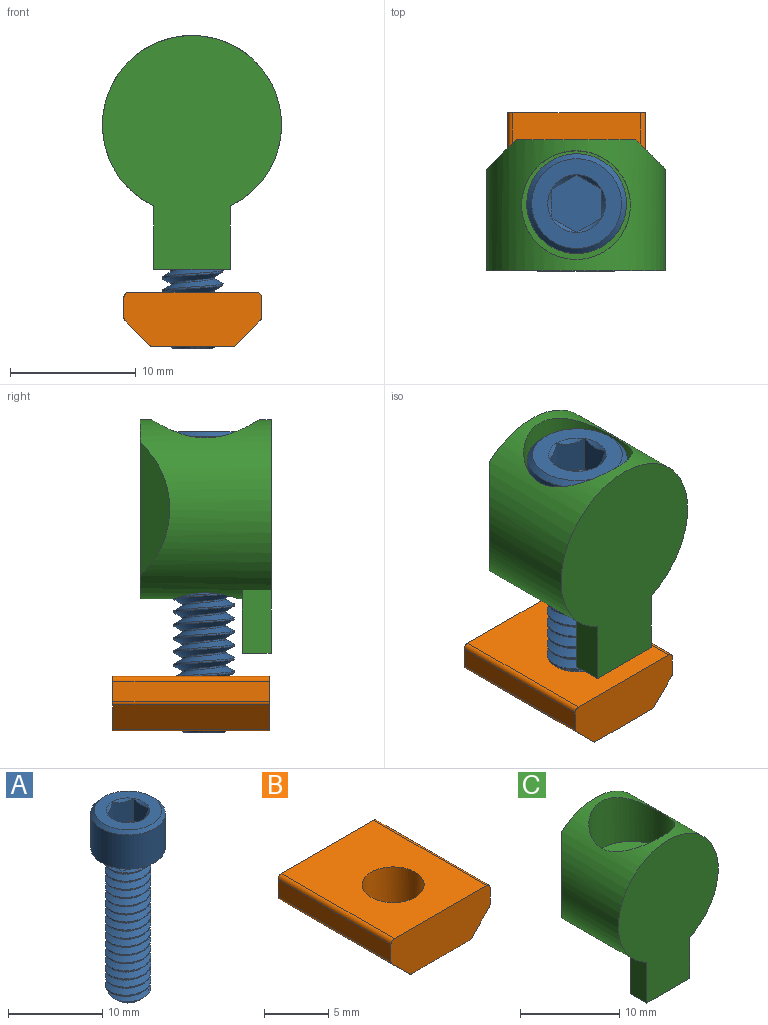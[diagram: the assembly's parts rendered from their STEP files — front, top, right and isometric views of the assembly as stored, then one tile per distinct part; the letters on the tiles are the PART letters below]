
ASSEMBLY  parts=3 mates=3
PART A: 23 faces, bbox 8.3x8.3x24.7 mm
  f0: cylinder r=2.41mm len=18.25mm, axis (0,0,1), area 34.7mm2, adj f1,f2,f4,f8
  f1: bspline ~20.01x4.94mm, area 181.7mm2, adj f0,f3,f4,f8
  f2: bspline ~19.48x4.94mm, area 181.9mm2, adj f0,f3,f4,f8
  f3: cylinder r=1.73mm len=18.94mm, axis (0,0,1), area 25.8mm2, adj f1,f2,f4,f8
  f4: cone r=1.61mm half-angle=45deg, axis (0,0,1), area 7.8mm2, adj f0,f1,f2,f3,f5
  f5: plane 3.22x3.22mm, normal (0,0,-1), area 8.2mm2, adj f4
  f6: cylinder r=3.96mm len=7.92mm, axis (0,0,-1), area 110.3mm2, adj f8,f22
  f7: plane 7.13x7.13mm, normal (0,0,1), area 23.5mm2, adj f9,f10,f11,f12,f13,f14,f22
  f8: plane 8.33x8.33mm, normal (0,0,-1), area 35.7mm2, adj f0,f1,f2,f3,f6
  f9: cone r=2.29mm half-angle=45deg, axis (0,0,1), area 0.7mm2, adj f7,f16
  f10: cone r=2.29mm half-angle=45deg, axis (0,0,1), area 0.7mm2, adj f7,f17
  f11: cone r=2.29mm half-angle=45deg, axis (0,0,1), area 0.7mm2, adj f7,f18
  f12: cone r=2.29mm half-angle=45deg, axis (0,0,1), area 0.7mm2, adj f7,f19
  f13: cone r=2.29mm half-angle=45deg, axis (0,0,1), area 0.7mm2, adj f7,f20
  f14: cone r=2.29mm half-angle=45deg, axis (0,0,1), area 0.7mm2, adj f7,f21
  f15: plane 4.58x3.97mm, normal (0,0,1), area 13.6mm2, adj f16,f17,f18,f19,f20,f21
  f16: plane 2.98x1.98mm, normal (0.5,-0.87,0), area 6.4mm2, adj f9,f15,f17,f21
  f17: plane 2.98x2.3mm, normal (1,0,0), area 6.4mm2, adj f10,f15,f16,f18
  f18: plane 2.98x1.98mm, normal (0.5,0.87,0), area 6.4mm2, adj f11,f15,f17,f19
  f19: plane 2.98x1.98mm, normal (-0.5,0.87,0), area 6.4mm2, adj f12,f15,f18,f20
  f20: plane 2.98x2.3mm, normal (-1,0,0), area 6.4mm2, adj f13,f15,f19,f21
  f21: plane 2.98x1.98mm, normal (-0.5,-0.87,0), area 6.4mm2, adj f14,f15,f16,f20
  f22: cone r=3.57mm half-angle=45deg, axis (0,0,-1), area 13.3mm2, adj f6,f7
PART B: 15 faces, bbox 10.9x12.4x4.3 mm
  f0: plane 12.45x1.94mm, normal (-0.71,0,-0.71), area 34.1mm2, adj f6,f7,f10,f13
  f1: plane 12.45x1.62mm, normal (-1,0,0), area 20.2mm2, adj f6,f7,f13,f14
  f2: plane 12.45x10.16mm, normal (0,0,1), area 108.2mm2, adj f6,f7,f8,f12,f14
  f3: plane 12.45x1.62mm, normal (1,0,0), area 20.2mm2, adj f6,f7,f11,f12
  f4: plane 12.45x1.94mm, normal (0.71,0,-0.71), area 34.1mm2, adj f6,f7,f9,f11
  f5: plane 12.45x6.29mm, normal (0,0,-1), area 60mm2, adj f6,f7,f8,f9,f10
  f6: plane 10.92x4.32mm, normal (0,1,0), area 42.4mm2, adj f0,f1,f2,f3,f4,f5,f9,f10
  f7: plane 10.92x4.32mm, normal (0,-1,0), area 42.4mm2, adj f0,f1,f2,f3,f4,f5,f9,f10
  f8: cylinder r=2.41mm len=4.83mm, axis (0,0,1), area 65.5mm2, adj f2,f5
  f9: cylinder r=0.38mm len=12.45mm, axis (0,-1,0), area 3.7mm2, adj f4,f5,f6,f7
  f10: cylinder r=0.38mm len=12.45mm, axis (0,-1,0), area 3.7mm2, adj f0,f5,f6,f7
  f11: cylinder r=0.38mm len=12.45mm, axis (0,-1,0), area 3.7mm2, adj f3,f4,f6,f7
  f12: cylinder r=0.38mm len=12.45mm, axis (0,-1,0), area 7.4mm2, adj f2,f3,f6,f7
  f13: cylinder r=0.38mm len=12.45mm, axis (0,-1,0), area 3.7mm2, adj f0,f1,f6,f7
  f14: cylinder r=0.38mm len=12.45mm, axis (0,-1,0), area 7.4mm2, adj f1,f2,f6,f7
PART C: 12 faces, bbox 14.2x10.4x18.6 mm
  f0: cylinder r=7.11mm len=14.22mm, axis (0,1,0), area 331.4mm2, adj f1,f2,f3,f5,f6,f7,f8,f9
  f1: plane 18.57x14.22mm, normal (0,-1,0), area 186.7mm2, adj f0,f3,f4,f5
  f2: plane 14.22x9.5mm, normal (0,1,0), area 124.3mm2, adj f0,f7,f8
  f3: plane 5.03x2.29mm, normal (1,0,0), area 11.5mm2, adj f0,f1,f4,f6
  f4: plane 6.09x2.29mm, normal (0,0,-1), area 13.9mm2, adj f1,f3,f5,f6
  f5: plane 5.03x2.29mm, normal (-1,0,0), area 11.5mm2, adj f0,f1,f4,f6
  f6: plane 6.09x5.03mm, normal (0,1,0), area 27.8mm2, adj f0,f3,f4,f5
  f7: plane 10.59x2.36mm, normal (-0.71,0.71,0), area 24.5mm2, adj f0,f2
  f8: plane 10.59x2.36mm, normal (0.71,0.71,0), area 24.5mm2, adj f0,f2
  f9: cylinder r=4.32mm len=8.64mm, axis (0,0,-1), area 138.6mm2, adj f0,f10
  f10: plane 8.64x8.64mm, normal (0,0,1), area 38.3mm2, adj f9,f11
  f11: cylinder r=2.54mm len=8.41mm, axis (0,0,1), area 130.5mm2, adj f0,f10
PLACE A t=(0.05,0.12,0)mm
PLACE B t=(0.05,0.12,-0.72)mm
PLACE C at identity
MATE cylindrical B.f8 <-> A.f0  axis (0,0,1) through (0.05,0.12,-14.59)mm
MATE parallel B.f3 <-> C.f3  axis (1,0,0) through (5.51,1.14,-15.78)mm
MATE fastened A.f8 <-> C.f9  axis (0,0,-1) through (0,0,0)mm
